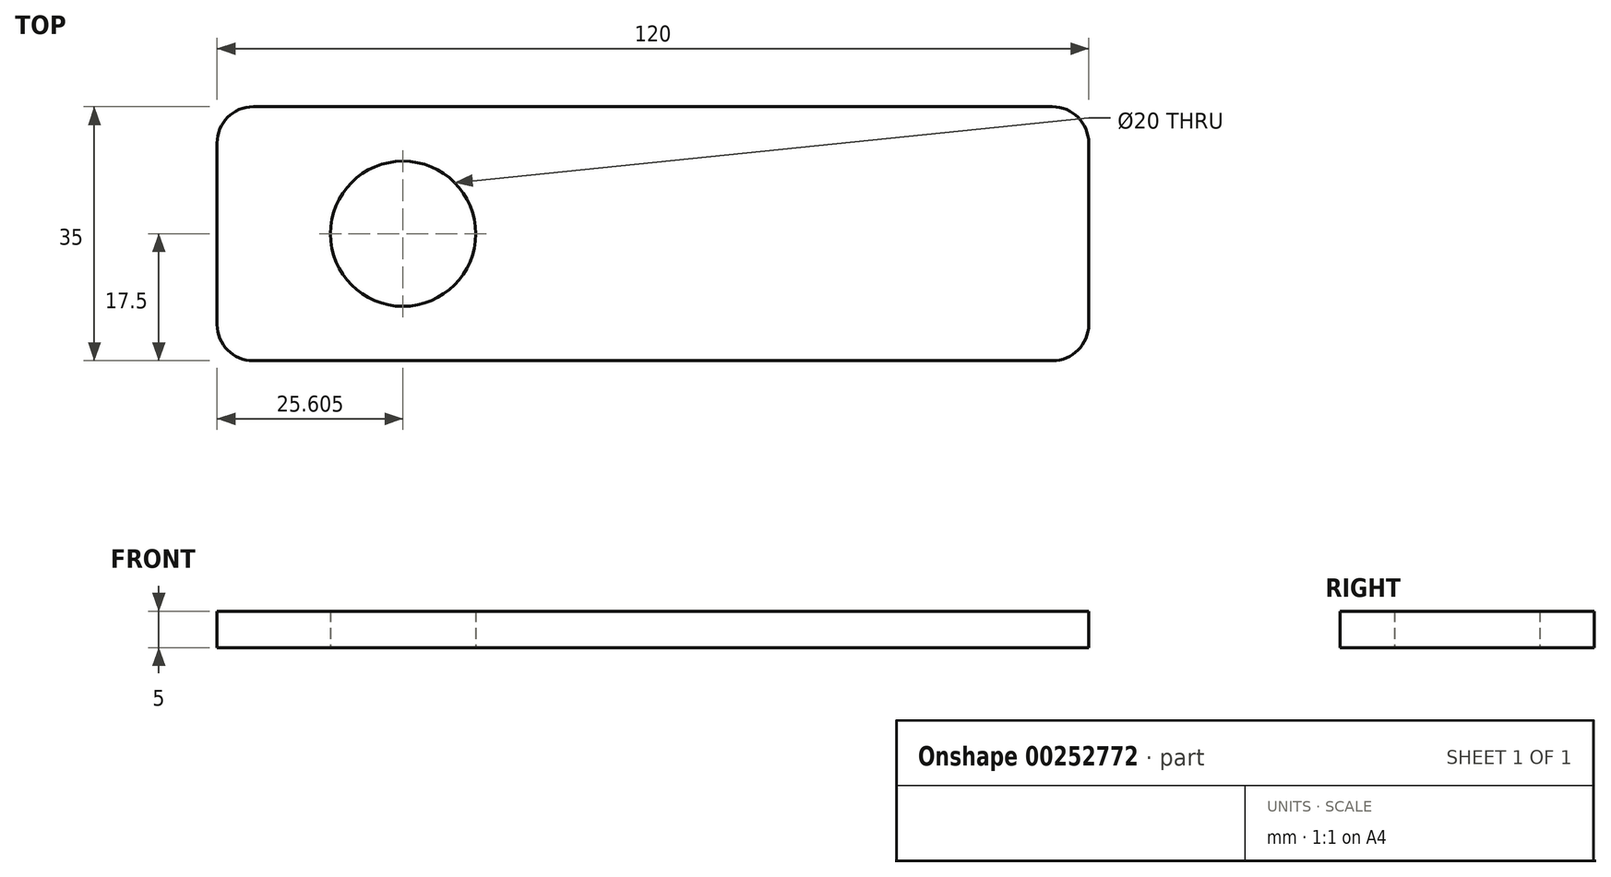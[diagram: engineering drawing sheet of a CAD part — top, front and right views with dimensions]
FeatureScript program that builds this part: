
annotation { "Feature Type Name" : "Feature", "Feature Type Description" : "" }
export const myFeature = defineFeature(function(context is Context, id is Id, definition is map)
    precondition{}
    {
        {
            var Q0;
            Q0=qCreatedBy(makeId("Top.planeOp"),FACE);
            var sketch = newSketch(context, id + "F0", { "sketchPlane" : qUnion([Q0])});
            skLineSegment(sketch, "E0.bottom", {"start": v(-60, 17.5) * mm, "end": v(60, 17.5) * mm});
            skLineSegment(sketch, "E0.top", {"start": v(-60, -17.5) * mm, "end": v(60, -17.5) * mm});
            skLineSegment(sketch, "E0.left", {"start": v(-60, 17.5) * mm, "end": v(-60, -17.5) * mm});
            skLineSegment(sketch, "E0.right", {"start": v(60, 17.5) * mm, "end": v(60, -17.5) * mm});
            skPoint(sketch, "E0.middle", {"position": v(0, 0) * mm});
            skCircle(sketch, "E1", {"center": v(-34.4, 0) * mm, "radius": 10 * mm});
            skSolve(sketch);
        }
        {
            var Q0;
            Q0=makeQuery(id+"F0.imprint","IMPRINT",FACE,{"disambiguationData":[TD([[makeQuery(id+"F0.imprint","IMPRINT",EDGE,{"derivedFrom":sQuery(id+"F0.wireOp",EDGE,"E0.bottom")}),-1.0]])]});
            extrude(context, id + "F1", {"entities" : qUnion([Q0]), "depth" : 5 * mm});
        }
        {
            var Q0;
            Q0=makeQuery(id+"F1.opExtrude","SWEPT_EDGE",EDGE,{"disambiguationData":[OSD([sQuery(id+"F0.wireOp",EDGE,"E0.top"),sQuery(id+"F0.wireOp",EDGE,"E0.left")])]});
            var Q1;
            Q1=makeQuery(id+"F1.opExtrude","SWEPT_EDGE",EDGE,{"disambiguationData":[OSD([sQuery(id+"F0.wireOp",EDGE,"E0.bottom"),sQuery(id+"F0.wireOp",EDGE,"E0.right")])]});
            var Q2;
            Q2=makeQuery(id+"F1.opExtrude","SWEPT_EDGE",EDGE,{"disambiguationData":[OSD([sQuery(id+"F0.wireOp",EDGE,"E0.top"),sQuery(id+"F0.wireOp",EDGE,"E0.right")])]});
            var Q3;
            Q3=makeQuery(id+"F1.opExtrude","SWEPT_EDGE",EDGE,{"disambiguationData":[OSD([sQuery(id+"F0.wireOp",EDGE,"E0.bottom"),sQuery(id+"F0.wireOp",EDGE,"E0.left")])]});
            fillet(context, id + "F2", {"entities" : qUnion([Q0, Q1, Q2, Q3]), "radius" : 5 * mm, "tangentPropagation" : true, "allowEdgeOverflow" : false});
        }
    });
